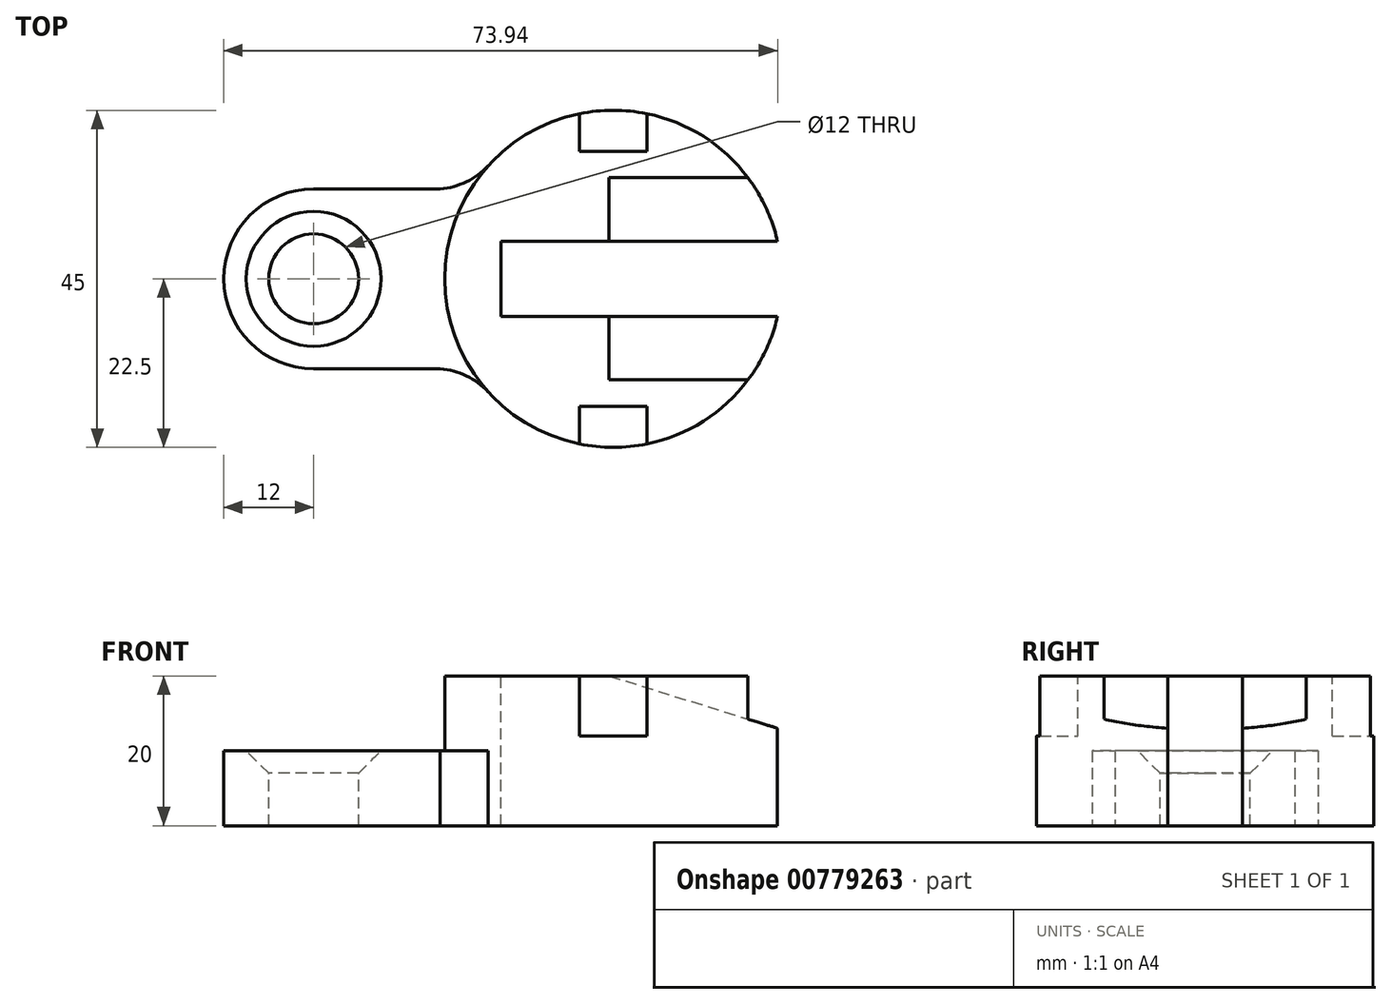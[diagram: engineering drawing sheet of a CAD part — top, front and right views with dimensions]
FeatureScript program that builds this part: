
annotation { "Feature Type Name" : "Feature", "Feature Type Description" : "" }
export const myFeature = defineFeature(function(context is Context, id is Id, definition is map)
    precondition{}
    {
        {
            var Q0;
            Q0=qCreatedBy(makeId("Top.planeOp"),FACE);
            var sketch = newSketch(context, id + "F0", { "sketchPlane" : qUnion([Q0])});
            skCircle(sketch, "E0", {"center": v(0, 0) * mm, "radius": 22.5 * mm});
            skLineSegment(sketch, "E1", {"start": v(0, 0) * mm, "end": v(-40, 0) * mm});
            skCircle(sketch, "E2", {"center": v(-40, 0) * mm, "radius": 12 * mm});
            skLineSegment(sketch, "E3", {"start": v(-40, 12) * mm, "end": v(-19.03, 12) * mm});
            skLineSegment(sketch, "E4", {"start": v(-40, -12) * mm, "end": v(-19.03, -12) * mm});
            skArc(sketch, "E5", {"start": v(-24.81, 12) * mm, "mid": v(-20.25, 12.67) * mm, "end": v(-16.48, 15.32) * mm});
            skLineSegment(sketch, "E6", {"start": v(-24.81, 12) * mm, "end": v(-24.81, -12) * mm});
            skLineSegment(sketch, "E7", {"start": v(-16.48, 15.32) * mm, "end": v(-16.48, -15.32) * mm});
            skArc(sketch, "E8", {"start": v(-16.48, -15.32) * mm, "mid": v(-20.25, -12.67) * mm, "end": v(-24.81, -12) * mm});
            skSolve(sketch);
        }
        {
            var Q0;
            Q0 = qSketchRegion(id + "F0", true);
            extrude(context, id + "F1", {"entities" : qUnion([Q0]), "depth" : 10 * mm, "offsetDistance" : 25.4 * mm});
        }
        {
            var Q0;
            Q0=makeQuery(id+"F1.opExtrude","CAP_FACE",FACE,{"disambiguationData":[OSD([sQuery(id+"F0.wireOp",EDGE,"E0"),sQuery(id+"F0.wireOp",EDGE,"E2"),sQuery(id+"F0.wireOp",EDGE,"E3"),sQuery(id+"F0.wireOp",EDGE,"E4"),sQuery(id+"F0.wireOp",EDGE,"E5"),sQuery(id+"F0.wireOp",EDGE,"E8")])],"isStart":false});
            var sketch = newSketch(context, id + "F2", { "sketchPlane" : qUnion([Q0])});
            skCircle(sketch, "E9", {"center": v(0, 0) * mm, "radius": 22.5 * mm});
            skSolve(sketch);
        }
        {
            var Q0;
            Q0 = qSketchRegion(id + "F2", true);
            extrude(context, id + "F3", {"entities" : qUnion([Q0]), "operationType" : NewBodyOperationType.ADD, "depth" : 10 * mm, "offsetDistance" : 25.4 * mm});
        }
        {
            var Q0;
            Q0=makeQuery(id+"F3.opExtrude","CAP_FACE",FACE,{"disambiguationData":[OSD([sQuery(id+"F2.wireOp",EDGE,"E9")])],"isStart":false});
            var sketch = newSketch(context, id + "F4", { "sketchPlane" : qUnion([Q0])});
            skLineSegment(sketch, "E10", {"start": v(0, 0) * mm, "end": v(-40, 0) * mm});
            skCircle(sketch, "E11", {"center": v(-40, 0) * mm, "radius": 6 * mm});
            skSolve(sketch);
        }
        {
            var Q0;
            Q0 = qSketchRegion(id + "F4", true);
            extrude(context, id + "F5", {"entities" : qUnion([Q0]), "operationType" : NewBodyOperationType.REMOVE, "endBound" : BoundingType.THROUGH_ALL, "oppositeDirection" : true, "depth" : 25.4 * mm, "offsetDistance" : 25.4 * mm});
        }
        {
            var Q0;
            Q0=makeQuery(id+"F5.boolean.opBoolean","INTERSECT",EDGE,{"derivedFrom":[makeQuery(id+"F1.opExtrude","CAP_FACE",FACE,{"disambiguationData":[OSD([sQuery(id+"F0.wireOp",EDGE,"E0"),sQuery(id+"F0.wireOp",EDGE,"E2"),sQuery(id+"F0.wireOp",EDGE,"E3"),sQuery(id+"F0.wireOp",EDGE,"E4"),sQuery(id+"F0.wireOp",EDGE,"E5"),sQuery(id+"F0.wireOp",EDGE,"E8")])],"isStart":false}),makeQuery(id+"F5.opExtrude","SWEPT_FACE",FACE,{"disambiguationData":[OSD([sQuery(id+"F4.wireOp",EDGE,"E11")])]})]});
            chamfer(context, id + "F6", {"entities" : qUnion([Q0]), "width" : 3 * mm, "tangentPropagation" : true});
        }
        {
            var Q0;
            Q0=makeQuery(id+"F3.opExtrude","CAP_FACE",FACE,{"disambiguationData":[OSD([sQuery(id+"F2.wireOp",EDGE,"E9")])],"isStart":false});
            var sketch = newSketch(context, id + "F7", { "sketchPlane" : qUnion([Q0])});
            skLineSegment(sketch, "E12.bottom", {"start": v(-15, -5) * mm, "end": v(60, -5) * mm});
            skLineSegment(sketch, "E12.top", {"start": v(-15, 5) * mm, "end": v(60, 5) * mm});
            skLineSegment(sketch, "E12.left", {"start": v(-15, -5) * mm, "end": v(-15, 5) * mm});
            skLineSegment(sketch, "E12.right", {"start": v(60, -5) * mm, "end": v(60, 5) * mm});
            skPoint(sketch, "E12.middle", {"position": v(22.5, 0) * mm});
            skLineSegment(sketch, "E13", {"start": v(-22.5, 0) * mm, "end": v(-15, 0) * mm});
            skPoint(sketch, "E13.startSnap0", {"position": v(-15, 0) * mm});
            skSolve(sketch);
        }
        {
            var Q0;
            Q0 = qSketchRegion(id + "F7", true);
            extrude(context, id + "F8", {"entities" : qUnion([Q0]), "operationType" : NewBodyOperationType.REMOVE, "endBound" : BoundingType.THROUGH_ALL, "oppositeDirection" : true, "depth" : 25.4 * mm, "offsetDistance" : 25.4 * mm});
        }
        {
            var Q0;
            Q0=makeQuery(id+"F3.opExtrude","CAP_FACE",FACE,{"disambiguationData":[OSD([sQuery(id+"F2.wireOp",EDGE,"E9")])],"isStart":false});
            var sketch = newSketch(context, id + "F9", { "sketchPlane" : qUnion([Q0])});
            skLineSegment(sketch, "E14.bottom", {"start": v(-4.5, -28) * mm, "end": v(4.5, -28) * mm});
            skLineSegment(sketch, "E14.top", {"start": v(-4.5, -17) * mm, "end": v(4.5, -17) * mm});
            skLineSegment(sketch, "E14.left", {"start": v(-4.5, -28) * mm, "end": v(-4.5, -17) * mm});
            skLineSegment(sketch, "E14.right", {"start": v(4.5, -28) * mm, "end": v(4.5, -17) * mm});
            skPoint(sketch, "E14.middle", {"position": v(0, -22.5) * mm});
            skLineSegment(sketch, "E15.bottom", {"start": v(-4.5, 17) * mm, "end": v(4.5, 17) * mm});
            skLineSegment(sketch, "E15.top", {"start": v(-4.5, 28) * mm, "end": v(4.5, 28) * mm});
            skLineSegment(sketch, "E15.left", {"start": v(-4.5, 17) * mm, "end": v(-4.5, 28) * mm});
            skLineSegment(sketch, "E15.right", {"start": v(4.5, 17) * mm, "end": v(4.5, 28) * mm});
            skPoint(sketch, "E15.middle", {"position": v(0, 22.5) * mm});
            skLineSegment(sketch, "E16", {"start": v(0, 22.5) * mm, "end": v(0, 17) * mm});
            skLineSegment(sketch, "E17", {"start": v(0, -22.5) * mm, "end": v(0, -28) * mm});
            skSolve(sketch);
        }
        {
            var Q0;
            Q0 = qSketchRegion(id + "F9", true);
            extrude(context, id + "F10", {"entities" : qUnion([Q0]), "operationType" : NewBodyOperationType.REMOVE, "oppositeDirection" : true, "depth" : 8 * mm, "offsetDistance" : 25.4 * mm});
        }
        {
            var Q0;
            Q0=makeQuery(id+"F8.boolean.opBoolean","COPY",FACE,{"derivedFrom":makeQuery(id+"F8.opExtrude","SWEPT_FACE",FACE,{"disambiguationData":[OSD([sQuery(id+"F7.wireOp",EDGE,"E12.top")])]})});
            var sketch = newSketch(context, id + "F11", { "sketchPlane" : qUnion([Q0])});
            skLineSegment(sketch, "E18", {"start": v(21.94, 0) * mm, "end": v(21.94, 13) * mm});
            skLineSegment(sketch, "E19", {"start": v(21.94, 20) * mm, "end": v(21.94, 13) * mm});
            skLineSegment(sketch, "E20", {"start": v(21.94, 13) * mm, "end": v(-0.56, 13) * mm});
            skLineSegment(sketch, "E21", {"start": v(-0.56, 13) * mm, "end": v(-0.56, 20) * mm});
            skLineSegment(sketch, "E22", {"start": v(-0.56, 20) * mm, "end": v(21.94, 13) * mm});
            skSolve(sketch);
        }
        {
            var Q0;
            {var subQ0=sQuery(id+"F11.wireOp",EDGE,"E19");Q0=makeQuery(id+"F11.imprint","IMPRINT",FACE,{"disambiguationData":[TD([[makeQuery(id+"F11.imprint","IMPRINT",EDGE,{"derivedFrom":subQ0}),1.0]])]});}
            extrude(context, id + "F12", {"entities" : qUnion([Q0]), "operationType" : NewBodyOperationType.REMOVE, "oppositeDirection" : true, "depth" : 8.5 * mm, "offsetDistance" : 25.4 * mm});
        }
        {
            var Q0;
            Q0=makeQuery(id+"F8.boolean.opBoolean","COPY",FACE,{"derivedFrom":makeQuery(id+"F8.opExtrude","SWEPT_FACE",FACE,{"disambiguationData":[OSD([sQuery(id+"F7.wireOp",EDGE,"E12.bottom")])]})});
            var sketch = newSketch(context, id + "F13", { "sketchPlane" : qUnion([Q0])});
            skLineSegment(sketch, "E23", {"start": v(-21.94, 0) * mm, "end": v(-21.94, 13) * mm});
            skLineSegment(sketch, "E24", {"start": v(-21.94, 13) * mm, "end": v(-21.94, 20) * mm});
            skLineSegment(sketch, "E25", {"start": v(-21.94, 13) * mm, "end": v(0.56, 13) * mm});
            skLineSegment(sketch, "E26", {"start": v(0.56, 13) * mm, "end": v(0.56, 20) * mm});
            skLineSegment(sketch, "E27", {"start": v(0.56, 20) * mm, "end": v(-21.94, 13) * mm});
            skSolve(sketch);
        }
        {
            var Q0;
            {var subQ0=sQuery(id+"F13.wireOp",EDGE,"E24");Q0=makeQuery(id+"F13.imprint","IMPRINT",FACE,{"disambiguationData":[TD([[makeQuery(id+"F13.imprint","IMPRINT",EDGE,{"derivedFrom":subQ0}),-1.0]])]});}
            extrude(context, id + "F14", {"entities" : qUnion([Q0]), "operationType" : NewBodyOperationType.REMOVE, "oppositeDirection" : true, "depth" : 8.5 * mm, "offsetDistance" : 25.4 * mm});
        }
    });
